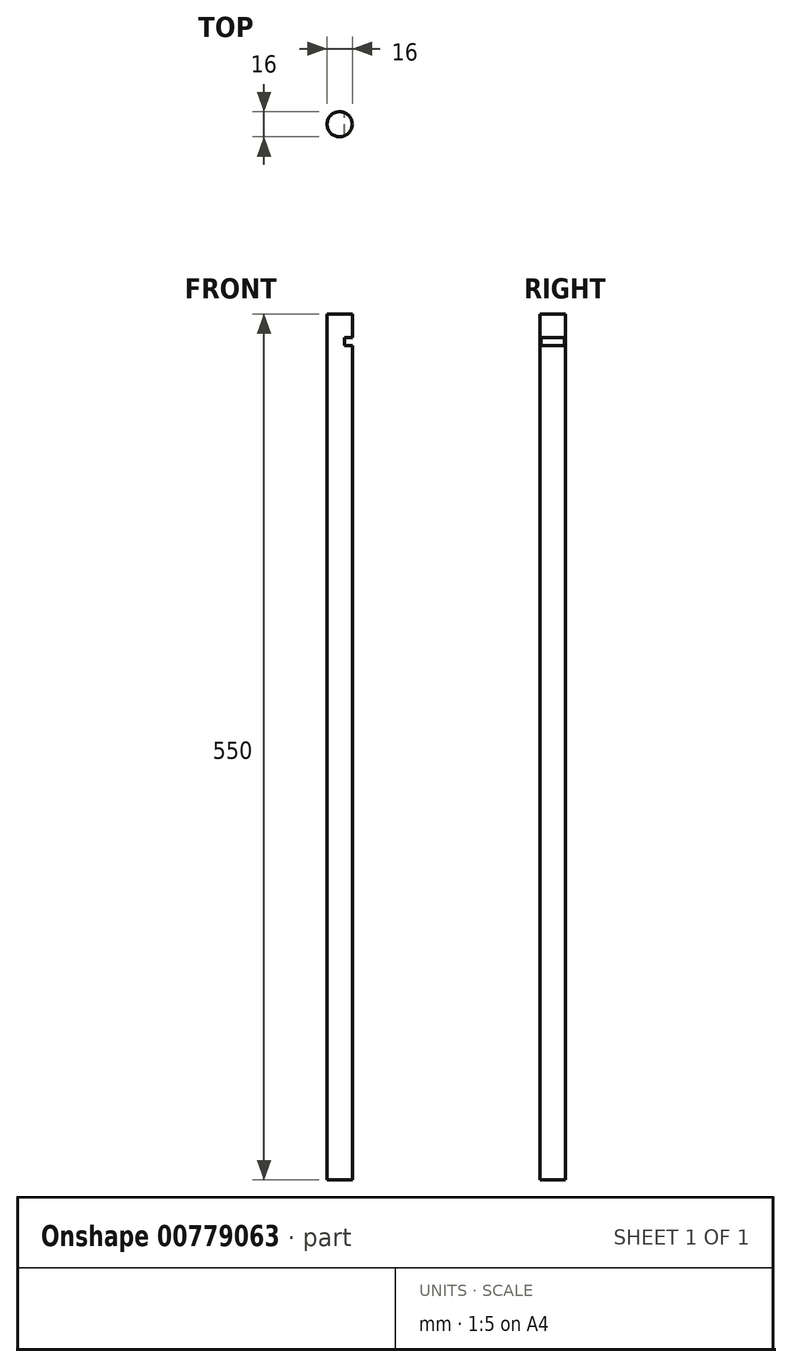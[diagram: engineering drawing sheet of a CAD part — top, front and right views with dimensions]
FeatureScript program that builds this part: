
annotation { "Feature Type Name" : "Feature", "Feature Type Description" : "" }
export const myFeature = defineFeature(function(context is Context, id is Id, definition is map)
    precondition{}
    {
        {
            var Q0;
            Q0=qCreatedBy(makeId("Top.planeOp"),FACE);
            var sketch = newSketch(context, id + "F0", { "sketchPlane" : qUnion([Q0])});
            skCircle(sketch, "E0", {"center": v(0, 0) * mm, "radius": 8 * mm});
            skSolve(sketch);
        }
        {
            var Q0;
            Q0=makeQuery(id+"F0.imprint","IMPRINT",FACE,{"disambiguationData":[TD([[makeQuery(id+"F0.imprint","IMPRINT",EDGE,{"derivedFrom":sQuery(id+"F0.wireOp",EDGE,"E0")}),1.0]])]});
            extrude(context, id + "F1", {"entities" : qUnion([Q0]), "depth" : 550 * mm, "offsetDistance" : 25 * mm});
        }
        {
            var Q0;
            Q0=qCreatedBy(makeId("Front.planeOp"),FACE);
            var sketch = newSketch(context, id + "F2", { "sketchPlane" : qUnion([Q0])});
            skLineSegment(sketch, "E1", {"start": v(8, 535) * mm, "end": v(3, 535) * mm});
            skLineSegment(sketch, "E2", {"start": v(3, 535) * mm, "end": v(3, 530) * mm});
            skLineSegment(sketch, "E3", {"start": v(3, 530) * mm, "end": v(8, 530) * mm});
            skLineSegment(sketch, "E4", {"start": v(8, 530) * mm, "end": v(8, 535) * mm});
            skSolve(sketch);
        }
        {
            var Q0;
            Q0 = qSketchRegion(id + "F2", true);
            extrude(context, id + "F3", {"entities" : qUnion([Q0]), "operationType" : NewBodyOperationType.REMOVE, "endBound" : BoundingType.SYMMETRIC, "depth" : 60 * mm, "offsetDistance" : 25 * mm});
        }
    });
